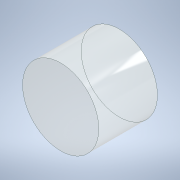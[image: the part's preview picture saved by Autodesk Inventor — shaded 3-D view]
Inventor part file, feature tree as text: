
AUTODESK INVENTOR PART (.ipt)
format: ipt  version: 2022 (Build 260153000, 153)  size: 104,960 bytes
history: native  units: in
note: dims shown in document units (in); Inventor stores cm internally (conversion verified against a paired STEP export)
features: extrude x1, sketch x1
ambient origin geometry x8: Origin, YZ Plane, XZ Plane, XY Plane, X Axis, Y Axis, Z Axis, Center Point
bodies: Body1 (feature_tree)
feature tree (2):
  extrude  "Extrusion1"  Depth=0.1969in
  sketch  "Sketch2"  dims[d1=0.2559in d2=0.2559in d3=0.1969in d4=0.0in]
